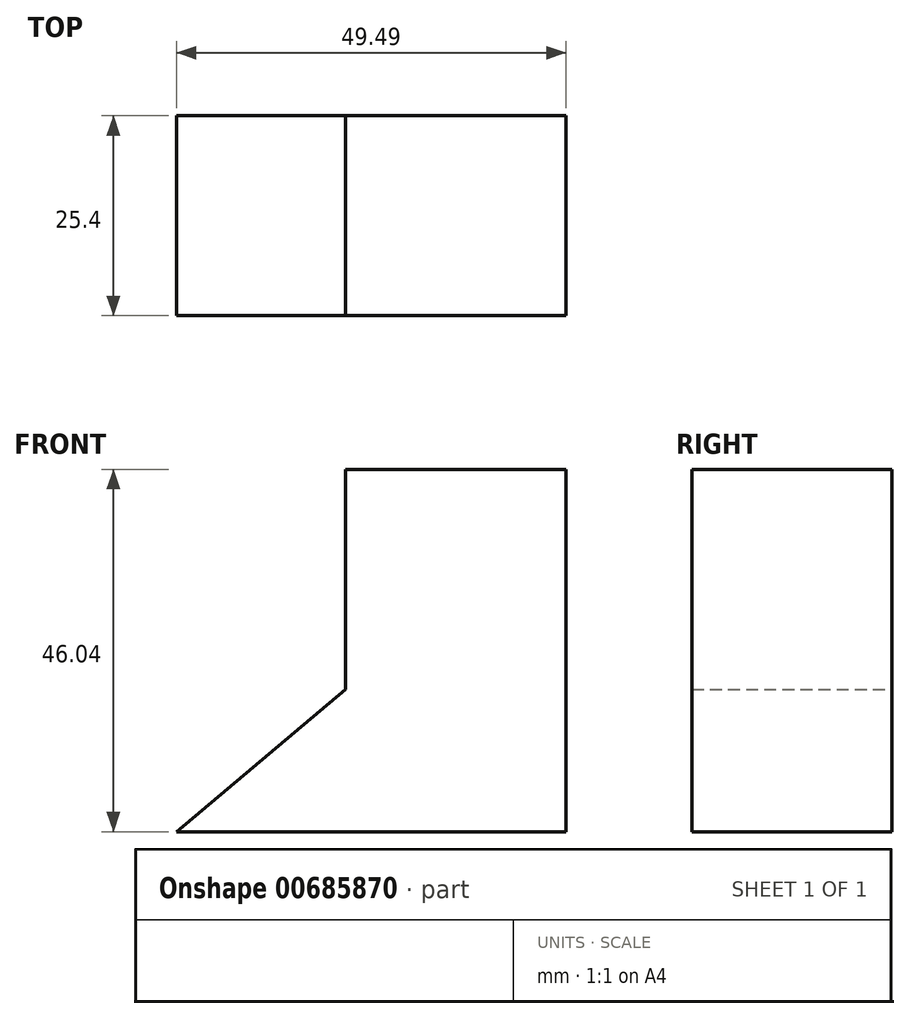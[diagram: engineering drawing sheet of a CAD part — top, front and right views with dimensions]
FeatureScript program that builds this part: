
annotation { "Feature Type Name" : "Feature", "Feature Type Description" : "" }
export const myFeature = defineFeature(function(context is Context, id is Id, definition is map)
    precondition{}
    {
        {
            var Q0;
            Q0=qCreatedBy(makeId("Front.planeOp"),FACE);
            var sketch = newSketch(context, id + "F0", { "sketchPlane" : qUnion([Q0])});
            skPoint(sketch, "E0.end.orphan", {"position": v(-35.29, 27.99) * mm});
            skPoint(sketch, "E1.end.orphan", {"position": v(0, 27.99) * mm});
            skLineSegment(sketch, "E2", {"start": v(0, 0) * mm, "end": v(21.5, 18.05) * mm});
            skLineSegment(sketch, "E3", {"start": v(21.5, 18.05) * mm, "end": v(21.5, 46.04) * mm});
            skLineSegment(sketch, "E4", {"start": v(21.5, 46.04) * mm, "end": v(49.49, 46.04) * mm});
            skLineSegment(sketch, "E5", {"start": v(49.49, 46.04) * mm, "end": v(49.49, 0) * mm});
            skLineSegment(sketch, "E6", {"start": v(0, 0) * mm, "end": v(49.49, 0) * mm});
            skSolve(sketch);
        }
        {
            var Q0;
            Q0 = qSketchRegion(id + "F0", true);
            extrude(context, id + "F1", {"entities" : qUnion([Q0]), "depth" : 25.4 * mm, "offsetDistance" : 25.4 * mm});
        }
    });
